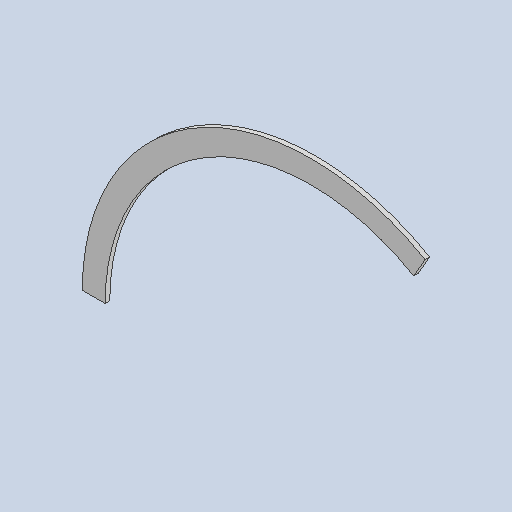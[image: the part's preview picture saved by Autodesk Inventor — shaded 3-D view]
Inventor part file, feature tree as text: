
AUTODESK INVENTOR PART (.ipt)
format: ipt  version: 2024.2 (Build 282272000, 272)  size: 267,264 bytes
history: native  units: mm
features: other x2, sheet_metal_op x1, sketch x1
ambient origin geometry x8: Origin, YZ Plane, XZ Plane, XY Plane, X Axis, Y Axis, Z Axis, Center Point
bodies: Solid1 (feature_tree)
feature tree (4):
  sheet_metal_op  "Face1"
  sketch  "Sketch1"  dims[d0=200.0mm d1=10.0mm d2=120.0deg d3=2.0mm]
  other  "Plate1"
  other  "Definition1"
